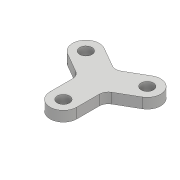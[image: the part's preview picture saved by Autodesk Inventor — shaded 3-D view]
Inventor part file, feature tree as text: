
AUTODESK INVENTOR PART (.ipt)
format: ipt  version: 2018 (Build 220112000, 112)  size: 113,152 bytes
history: native  units: mm
features: other x1, extrude x1, sketch x1
ambient origin geometry x8: Origin, YZ Plane, XZ Plane, XY Plane, X Axis, Y Axis, Z Axis, Center Point
bodies: Body1 (feature_tree)
feature tree (3):
  other  "實體1"
  extrude  "擠出1"  Depth=34.5mm
  sketch  "草圖1"
